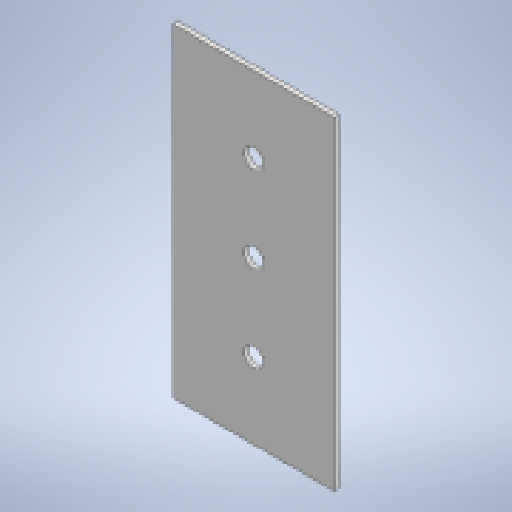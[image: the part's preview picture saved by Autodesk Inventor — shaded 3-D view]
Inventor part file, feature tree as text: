
AUTODESK INVENTOR PART (.ipt)
format: ipt  version: 2024 (Build 280153000, 153)  size: 137,216 bytes
history: native  units: mm
features: other x5, reference x2, extrude x1, sketch x1
ambient origin geometry x8: Origin, YZ Plane, XZ Plane, XY Plane, X Axis, Y Axis, Z Axis, Center Point
bodies: Body1 (feature_tree)
feature tree (9):
  other  "ソリッド1"
  extrude  "押し出し1"  Depth=6.0mm
  sketch  "スケッチ1"
  reference  "参照1"
  reference  "参照2"
  other  "<userpath>\OneDrive\ドキュメント\Inventor\Vixen\kosi.iam"
  other  "kosi.iam"
  other  "gia1:1"
  other  "gia1:2"
